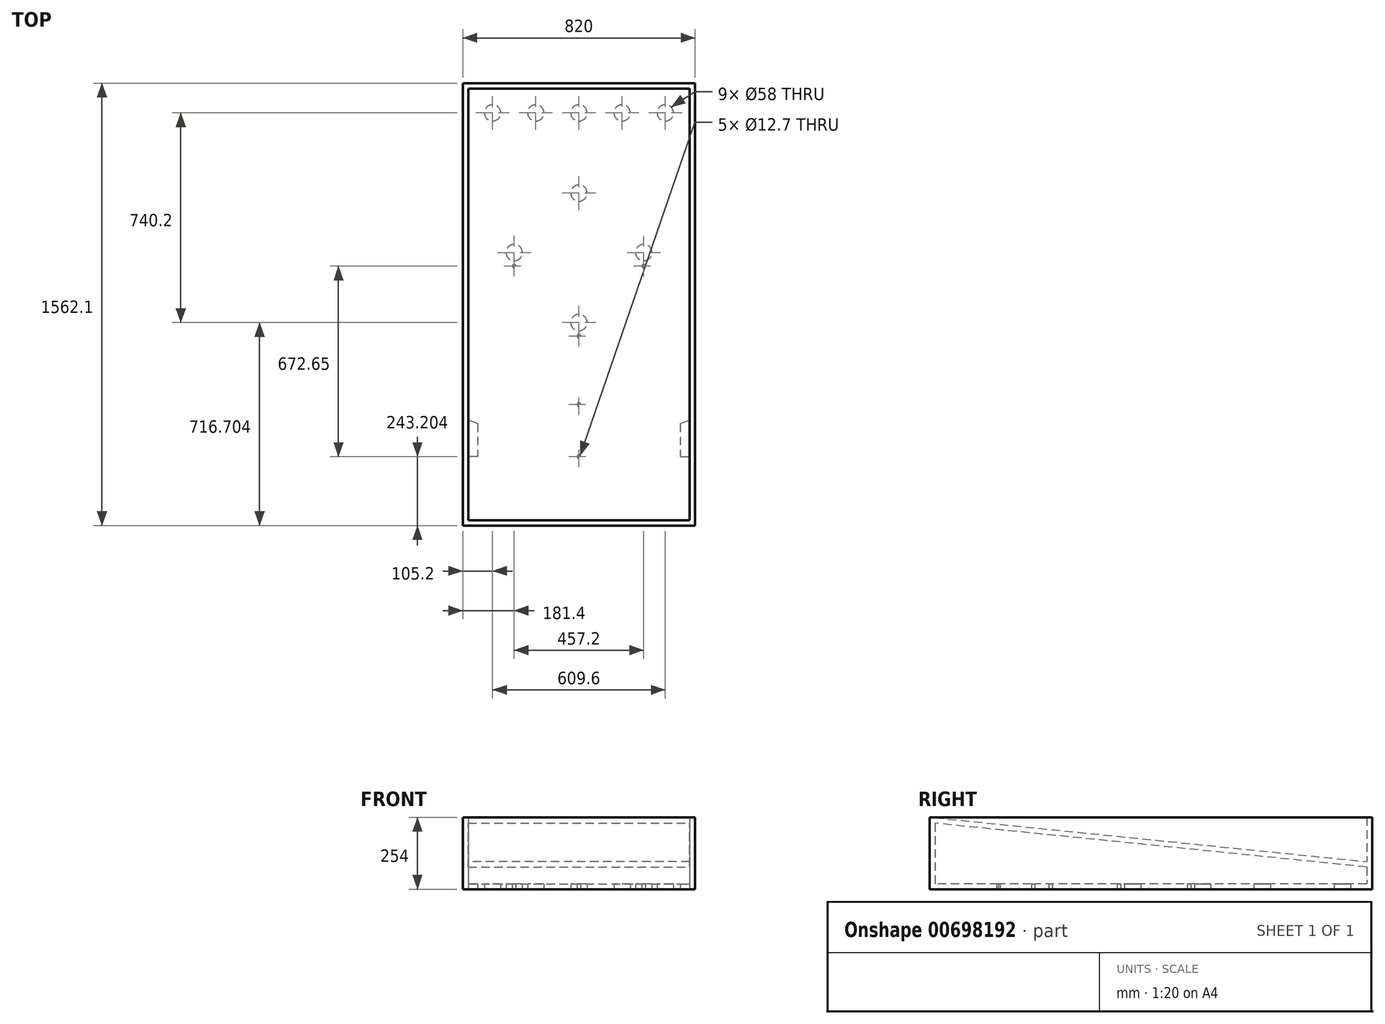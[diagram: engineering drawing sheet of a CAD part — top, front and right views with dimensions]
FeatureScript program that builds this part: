
annotation { "Feature Type Name" : "Feature", "Feature Type Description" : "" }
export const myFeature = defineFeature(function(context is Context, id is Id, definition is map)
    precondition{}
    {
        {
            var Q0;
            Q0=qCreatedBy(makeId("Top.planeOp"),FACE);
            var sketch = newSketch(context, id + "F0", { "sketchPlane" : qUnion([Q0])});
            skLineSegment(sketch, "E0.bottom", {"start": v(-390.95, 742.05) * mm, "end": v(390.95, 742.05) * mm});
            skLineSegment(sketch, "E0.top", {"start": v(-390.95, -781.95) * mm, "end": v(390.95, -781.95) * mm});
            skLineSegment(sketch, "E0.left", {"start": v(-390.95, 742.05) * mm, "end": v(-390.95, -781.95) * mm});
            skLineSegment(sketch, "E0.right", {"start": v(390.95, 742.05) * mm, "end": v(390.95, -781.95) * mm});
            skCircle(sketch, "E1", {"center": v(0, 655.9) * mm, "radius": 29 * mm});
            skCircle(sketch, "E2", {"center": v(152.4, 655.9) * mm, "radius": 29 * mm});
            skCircle(sketch, "E3", {"center": v(-152.4, 655.9) * mm, "radius": 29 * mm});
            skCircle(sketch, "E4", {"center": v(304.8, 655.9) * mm, "radius": 29 * mm});
            skCircle(sketch, "E5", {"center": v(-304.8, 655.9) * mm, "radius": 29 * mm});
            skCircle(sketch, "E6", {"center": v(0, 372.9) * mm, "radius": 29 * mm});
            skCircle(sketch, "E7", {"center": v(-228.6, 162.9) * mm, "radius": 29 * mm});
            skCircle(sketch, "E8", {"center": v(228.6, 162.9) * mm, "radius": 29 * mm});
            skCircle(sketch, "E9", {"center": v(0, -84.3) * mm, "radius": 29 * mm});
            skCircle(sketch, "E10", {"center": v(0, -132.35) * mm, "radius": 6.35 * mm});
            skCircle(sketch, "E11", {"center": v(228.6, 114.85) * mm, "radius": 6.35 * mm});
            skCircle(sketch, "E12", {"center": v(-228.6, 114.85) * mm, "radius": 6.35 * mm});
            skCircle(sketch, "E13", {"center": v(0, -373.65) * mm, "radius": 6.35 * mm});
            skCircle(sketch, "E14", {"center": v(0, -557.8) * mm, "radius": 6.35 * mm});
            skLineSegment(sketch, "E15", {"start": v(0, -557.8) * mm, "end": v(390.95, -557.8) * mm});
            skLineSegment(sketch, "E16", {"start": v(0, -557.8) * mm, "end": v(-390.95, -557.8) * mm});
            skArc(sketch, "E17", {"start": v(38.1, -557.8) * mm, "mid": v(0, -519.7) * mm, "end": v(-38.1, -557.8) * mm});
            skLineSegment(sketch, "E18", {"start": v(390.95, -557.8) * mm, "end": v(390.95, -429.27) * mm});
            skLineSegment(sketch, "E19", {"start": v(38.1, -557.8) * mm, "end": v(390.95, -429.27) * mm});
            skLineSegment(sketch, "E20", {"start": v(-390.95, -557.8) * mm, "end": v(-390.95, -429.27) * mm});
            skLineSegment(sketch, "E21", {"start": v(-38.1, -557.8) * mm, "end": v(-390.95, -429.27) * mm});
            skLineSegment(sketch, "E22.0", {"start": v(-357.93, 709.03) * mm, "end": v(-357.93, -748.93) * mm});
            skLineSegment(sketch, "E22.1", {"start": v(-357.93, 709.03) * mm, "end": v(357.93, 709.03) * mm});
            skLineSegment(sketch, "E22.2", {"start": v(357.93, 709.03) * mm, "end": v(357.93, -748.93) * mm});
            skLineSegment(sketch, "E22.3", {"start": v(-357.93, -748.93) * mm, "end": v(357.93, -748.93) * mm});
            skLineSegment(sketch, "E23.bottom", {"start": v(-410, 761.1) * mm, "end": v(410, 761.1) * mm});
            skLineSegment(sketch, "E23.top", {"start": v(-410, -801) * mm, "end": v(410, -801) * mm});
            skLineSegment(sketch, "E23.left", {"start": v(-410, 761.1) * mm, "end": v(-410, -801) * mm});
            skLineSegment(sketch, "E23.right", {"start": v(410, 761.1) * mm, "end": v(410, -801) * mm});
            skSolve(sketch);
        }
        {
            var Q0;
            Q0=makeQuery(id+"F0.imprint","IMPRINT",FACE,{"disambiguationData":[TD([[makeQuery(id+"F0.imprint","IMPRINT",EDGE,{"derivedFrom":sQuery(id+"F0.wireOp",EDGE,"E1")}),-1.0]])]});
            var Q1;
            {var subQ1=sQuery(id+"F0.wireOp",EDGE,"E15");var subQ3=sQuery(id+"F0.wireOp",EDGE,"E22.2");var subQ4=makeQuery(id+"F0.imprint","INTERSECT",VERTEX,{"derivedFrom":[subQ1,subQ3]});Q1=makeQuery(id+"F0.imprint","IMPRINT",FACE,{"disambiguationData":[TD([[makeQuery(id+"F0.imprint","IMPRINT",EDGE,{"disambiguationData":[TD([[subQ4,1.0]])],"derivedFrom":subQ3}),-1.0]])]});}
            var Q2;
            {var subQ1=sQuery(id+"F0.wireOp",EDGE,"E16");var subQ3=sQuery(id+"F0.wireOp",EDGE,"E22.0");var subQ4=makeQuery(id+"F0.imprint","INTERSECT",VERTEX,{"derivedFrom":[subQ1,subQ3]});Q2=makeQuery(id+"F0.imprint","IMPRINT",FACE,{"disambiguationData":[TD([[makeQuery(id+"F0.imprint","IMPRINT",EDGE,{"disambiguationData":[TD([[subQ4,1.0]])],"derivedFrom":subQ3}),1.0]])]});}
            var Q3;
            {var subQ10=sQuery(id+"F0.wireOp",EDGE,"E22.3");Q3=makeQuery(id+"F0.imprint","IMPRINT",FACE,{"disambiguationData":[TD([[makeQuery(id+"F0.imprint","IMPRINT",EDGE,{"derivedFrom":subQ10}),1.0]])]});}
            var Q4;
            {var subQ5=sQuery(id+"F0.wireOp",EDGE,"E17");Q4=makeQuery(id+"F0.imprint","IMPRINT",FACE,{"disambiguationData":[TD([[makeQuery(id+"F0.imprint","IMPRINT",EDGE,{"derivedFrom":subQ5}),1.0]])]});}
            var Q5;
            {var subQ1=sQuery(id+"F0.wireOp",EDGE,"E0.bottom");Q5=makeQuery(id+"F0.imprint","IMPRINT",FACE,{"disambiguationData":[TD([[makeQuery(id+"F0.imprint","IMPRINT",EDGE,{"derivedFrom":subQ1}),-1.0]])]});}
            var Q6;
            {var subQ0=sQuery(id+"F0.wireOp",EDGE,"E20");Q6=makeQuery(id+"F0.imprint","IMPRINT",FACE,{"disambiguationData":[TD([[makeQuery(id+"F0.imprint","IMPRINT",EDGE,{"derivedFrom":subQ0}),-1.0]])]});}
            var Q7;
            {var subQ5=sQuery(id+"F0.wireOp",EDGE,"E0.top");Q7=makeQuery(id+"F0.imprint","IMPRINT",FACE,{"disambiguationData":[TD([[makeQuery(id+"F0.imprint","IMPRINT",EDGE,{"derivedFrom":subQ5}),1.0]])]});}
            var Q8;
            {var subQ0=sQuery(id+"F0.wireOp",EDGE,"E18");Q8=makeQuery(id+"F0.imprint","IMPRINT",FACE,{"disambiguationData":[TD([[makeQuery(id+"F0.imprint","IMPRINT",EDGE,{"derivedFrom":subQ0}),1.0]])]});}
            extrude(context, id + "F1", {"entities" : qUnion([Q0, Q1, Q2, Q3, Q4, Q5, Q6, Q7, Q8]), "depth" : 19.05 * mm, "offsetDistance" : 25.4 * mm});
        }
        {
            var Q0;
            {var subQ3=sQuery(id+"F0.wireOp",EDGE,"E0.bottom");Q0=makeQuery(id+"F0.imprint","IMPRINT",FACE,{"disambiguationData":[TD([[makeQuery(id+"F0.imprint","IMPRINT",EDGE,{"derivedFrom":subQ3}),1.0]])]});}
            extrude(context, id + "F2", {"entities" : qUnion([Q0]), "operationType" : NewBodyOperationType.ADD, "depth" : 254 * mm, "offsetDistance" : 25.4 * mm});
        }
        {
            var Q0;
            Q0=makeQuery(id+"F2.opExtrude","SWEPT_FACE",FACE,{"disambiguationData":[OSD([sQuery(id+"F0.wireOp",EDGE,"E23.right")])]});
            var sketch = newSketch(context, id + "F3", { "sketchPlane" : qUnion([Q0])});
            skLineSegment(sketch, "E24", {"start": v(761.1, 76.2) * mm, "end": v(-801, 234.95) * mm});
            skLineSegment(sketch, "E25", {"start": v(-801, 234.95) * mm, "end": v(-801, 254) * mm});
            skLineSegment(sketch, "E26", {"start": v(-801, 254) * mm, "end": v(761.1, 95.25) * mm});
            skLineSegment(sketch, "E27", {"start": v(761.1, 95.25) * mm, "end": v(761.1, 76.2) * mm});
            skSolve(sketch);
        }
        {
            var Q0;
            Q0=makeQuery(id+"F3.imprint","IMPRINT",FACE,{"disambiguationData":[TD([[makeQuery(id+"F3.imprint","IMPRINT",EDGE,{"derivedFrom":sQuery(id+"F3.wireOp",EDGE,"E24")}),-1.0]])]});
            extrude(context, id + "F4", {"entities" : qUnion([Q0]), "operationType" : NewBodyOperationType.ADD, "depth" : -820 * mm, "offsetDistance" : 25.4 * mm});
        }
    });
